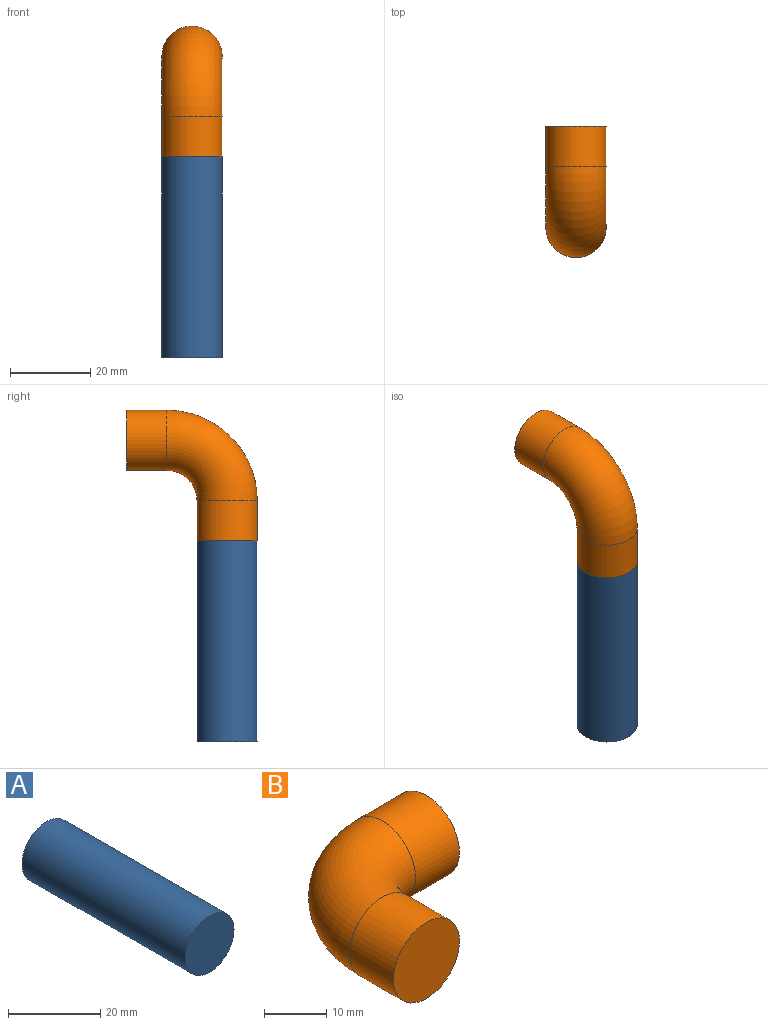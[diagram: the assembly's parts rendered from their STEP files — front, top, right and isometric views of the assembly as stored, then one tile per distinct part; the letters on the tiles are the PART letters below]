
ASSEMBLY  parts=2 mates=1
PART A: 3 faces, bbox 15x50x15 mm
  f0: cylinder r=7.5mm len=50mm, axis (0,1,0), area 2356.2mm2, adj f1,f2
  f1: plane 15x15mm, normal (0,-1,0), area 176.7mm2, adj f0
  f2: plane 15x15mm, normal (0,1,0), area 176.7mm2, adj f0
PART B: 5 faces, bbox 34.4x34.4x15 mm
  f0: plane 15x15mm, normal (0,-1,0), area 176.7mm2, adj f2
  f1: plane 15x15mm, normal (1,0,0), area 176.7mm2, adj f4
  f2: cylinder r=7.5mm len=15mm, axis (0,1,0), area 471.2mm2, adj f0,f3
  f3: torus R=15mm, axis (0,0,-1), area 1110.3mm2, adj f2,f4
  f4: cylinder r=7.5mm len=15mm, axis (1,0,0), area 471.2mm2, adj f1,f3
PLACE A rot(axis=(1,0,0),90deg) t=(11470,-5815,50)mm
PLACE B rot(axis=(0.58,0.58,0.58),120deg) t=(11470,-5815,50)mm
MATE revolute B.f2 <-> A.f0  axis (0,0,-1) through (11470,-5815,50)mm
